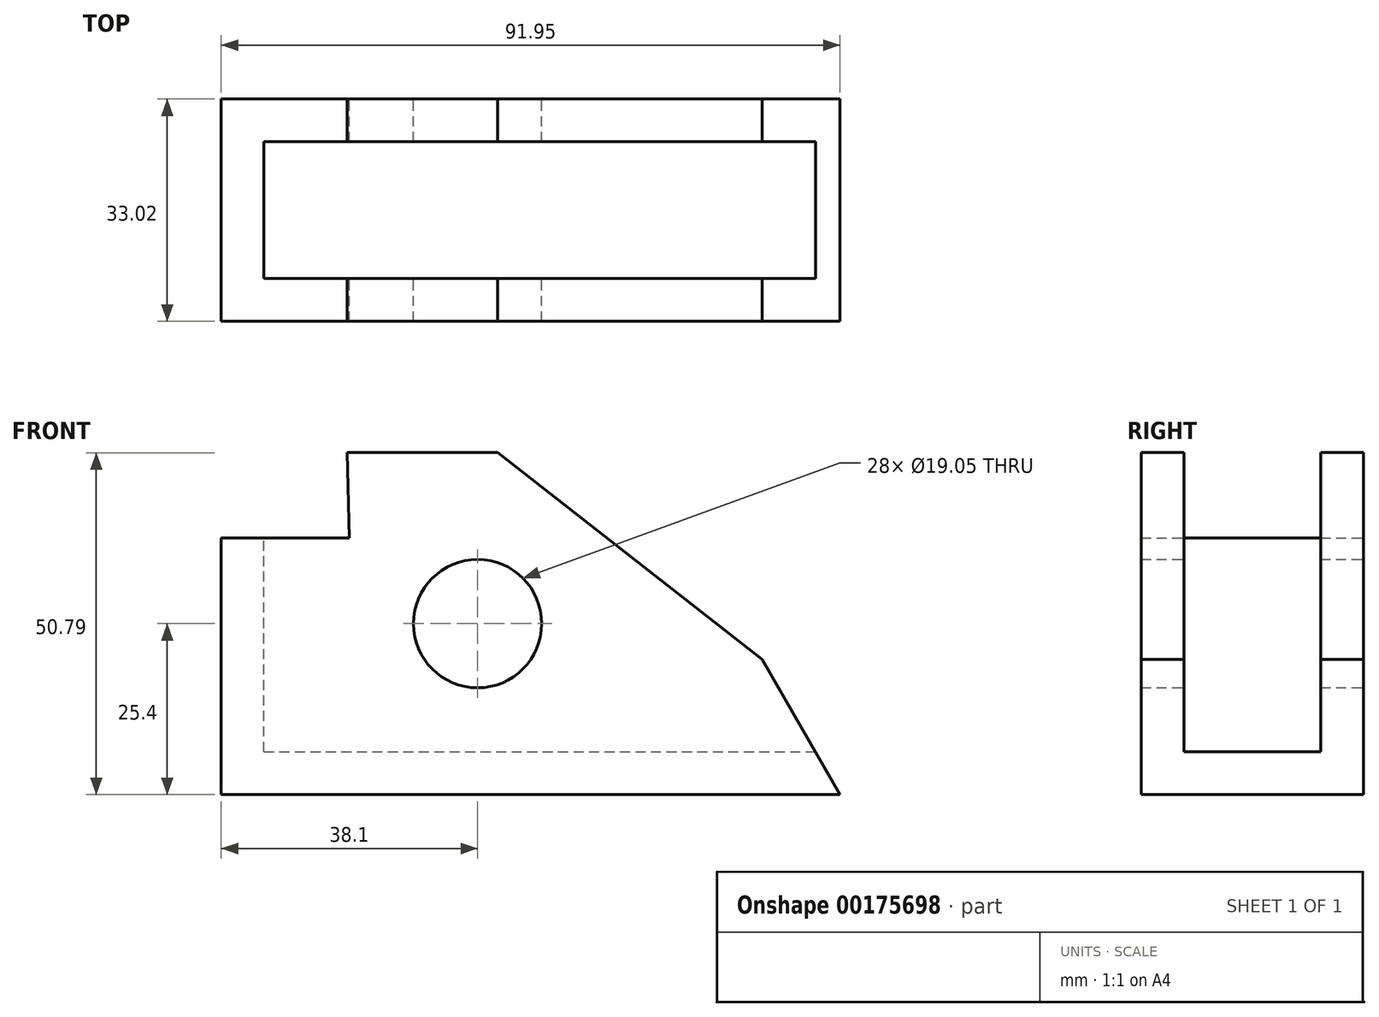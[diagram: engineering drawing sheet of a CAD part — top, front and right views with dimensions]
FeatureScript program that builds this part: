
annotation { "Feature Type Name" : "Feature", "Feature Type Description" : "" }
export const myFeature = defineFeature(function(context is Context, id is Id, definition is map)
    precondition{}
    {
        {
            var Q0;
            Q0=qCreatedBy(makeId("Front.planeOp"),FACE);
            var sketch = newSketch(context, id + "F0", { "sketchPlane" : qUnion([Q0])});
            skLineSegment(sketch, "E0", {"start": v(-19.4, 25.4) * mm, "end": v(2.94, 25.4) * mm});
            skLineSegment(sketch, "E1", {"start": v(42.25, -5.32) * mm, "end": v(2.94, 25.4) * mm});
            skLineSegment(sketch, "E2", {"start": v(42.25, -5.32) * mm, "end": v(53.85, -25.4) * mm});
            skLineSegment(sketch, "E3", {"start": v(53.85, -25.4) * mm, "end": v(-38.1, -25.4) * mm});
            skLineSegment(sketch, "E4", {"start": v(-38.1, -25.4) * mm, "end": v(-38.1, 12.7) * mm});
            skLineSegment(sketch, "E5", {"start": v(-38.1, 12.7) * mm, "end": v(-19.05, 12.7) * mm});
            skLineSegment(sketch, "E6", {"start": v(-19.05, 12.7) * mm, "end": v(-19.4, 25.4) * mm});
            skCircle(sketch, "E7", {"center": v(0, 0) * mm, "radius": 9.53 * mm});
            skSolve(sketch);
        }
        {
            var Q0;
            Q0=makeQuery(id+"F0.imprint","IMPRINT",FACE,{"disambiguationData":[TD([[makeQuery(id+"F0.imprint","IMPRINT",EDGE,{"derivedFrom":sQuery(id+"F0.wireOp",EDGE,"E0")}),-1.0]])]});
            extrude(context, id + "F1", {"entities" : qUnion([Q0]), "depth" : 33.02 * mm});
        }
        {
            var Q0;
            Q0=makeQuery(id+"F1.opExtrude","SWEPT_FACE",FACE,{"disambiguationData":[OSD([sQuery(id+"F0.wireOp",EDGE,"E0")])]});
            var sketch = newSketch(context, id + "F2", { "sketchPlane" : qUnion([Q0])});
            skPoint(sketch, "E8.firstSnap0", {"position": v(-19.4, -16.51) * mm});
            skLineSegment(sketch, "E8.bottom", {"start": v(-31.75, -26.67) * mm, "end": v(53.85, -26.67) * mm});
            skLineSegment(sketch, "E8.top", {"start": v(-31.75, -6.35) * mm, "end": v(53.85, -6.35) * mm});
            skLineSegment(sketch, "E8.left", {"start": v(-31.75, -26.67) * mm, "end": v(-31.75, -6.35) * mm});
            skLineSegment(sketch, "E8.right", {"start": v(53.85, -26.67) * mm, "end": v(53.85, -6.35) * mm});
            skSolve(sketch);
        }
        {
            var Q0;
            {var subQ0=sQuery(id+"F2.wireOp",EDGE,"E8.left");Q0=makeQuery(id+"F2.imprint","IMPRINT",FACE,{"disambiguationData":[TD([[makeQuery(id+"F2.imprint","IMPRINT",EDGE,{"derivedFrom":subQ0}),-1.0]])]});}
            var Q1;
            {var subQ0=sQuery(id+"F2.wireOp",EDGE,"E8.bottom");var subQ1=sQuery(id+"F0.wireOp",EDGE,"E0");var subQ2=makeQuery(id+"F1.opExtrude","SWEPT_EDGE",EDGE,{"disambiguationData":[OSD([subQ1,sQuery(id+"F0.wireOp",EDGE,"E6")])]});var subQ3=makeQuery(id+"F2.imprint","INTERSECT",VERTEX,{"derivedFrom":[subQ2,subQ0]});Q1=makeQuery(id+"F2.imprint","IMPRINT",FACE,{"disambiguationData":[TD([[makeQuery(id+"F2.imprint","IMPRINT",EDGE,{"disambiguationData":[TD([[subQ3,-1.0]])],"derivedFrom":subQ0}),1.0]])]});}
            var Q2;
            {var subQ0=sQuery(id+"F2.wireOp",EDGE,"E8.right");Q2=makeQuery(id+"F2.imprint","IMPRINT",FACE,{"disambiguationData":[TD([[makeQuery(id+"F2.imprint","IMPRINT",EDGE,{"derivedFrom":subQ0}),1.0]])]});}
            var Q3;
            {var subQ0=sQuery(id+"F2.wireOp",EDGE,"E8.right");Q3=makeQuery(id+"F2.imprint","IMPRINT",FACE,{"disambiguationData":[TD([[makeQuery(id+"F2.imprint","IMPRINT",EDGE,{"derivedFrom":subQ0}),1.0]])]});}
            extrude(context, id + "F3", {"entities" : qUnion([Q0, Q1, Q2, Q3]), "operationType" : NewBodyOperationType.REMOVE, "oppositeDirection" : true, "depth" : 44.45 * mm});
        }
    });
